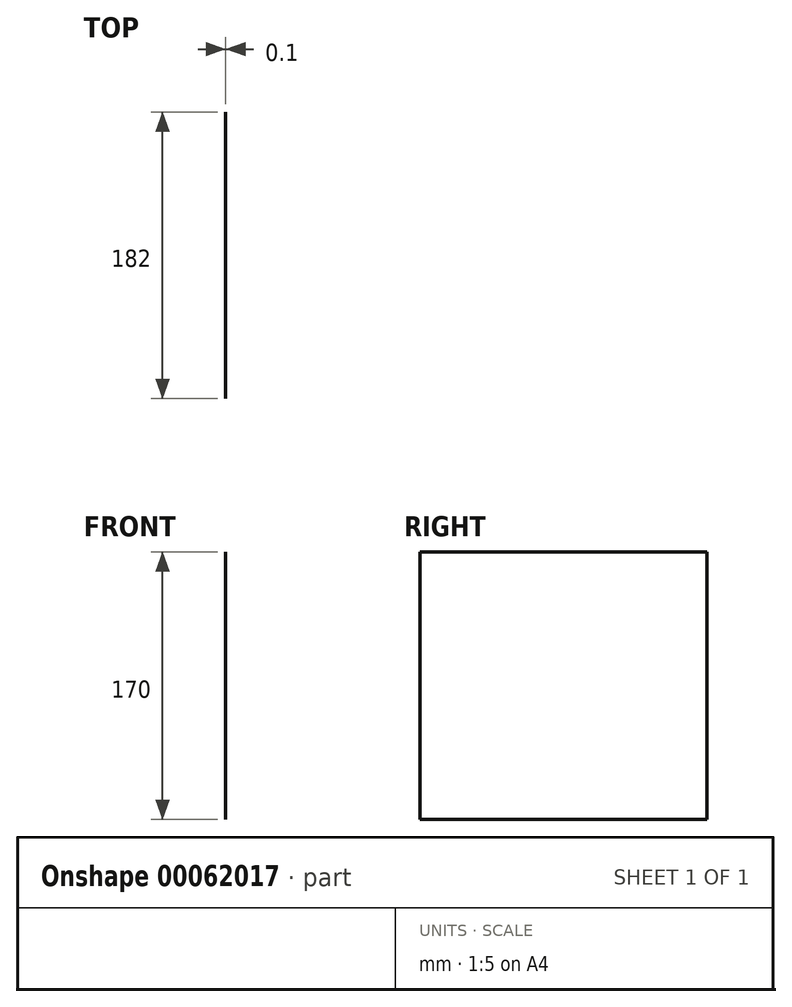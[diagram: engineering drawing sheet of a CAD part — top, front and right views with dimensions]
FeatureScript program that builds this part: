
annotation { "Feature Type Name" : "Feature", "Feature Type Description" : "" }
export const myFeature = defineFeature(function(context is Context, id is Id, definition is map)
    precondition{}
    {
        {
            var Q0;
            Q0=qCreatedBy(makeId("Front.planeOp"),FACE);
            var sketch = newSketch(context, id + "F0", { "sketchPlane" : qUnion([Q0])});
            skLineSegment(sketch, "E0", {"start": v(0, 72.34) * mm, "end": v(0, -97.66) * mm, "construction": true});
            skLineSegment(sketch, "E1.bottom", {"start": v(0, 72.34) * mm, "end": v(-0.1, 72.34) * mm});
            skLineSegment(sketch, "E1.top", {"start": v(0, -97.66) * mm, "end": v(-0.1, -97.66) * mm});
            skLineSegment(sketch, "E1.left", {"start": v(0, 72.34) * mm, "end": v(0, -97.66) * mm});
            skLineSegment(sketch, "E1.right", {"start": v(-0.1, 72.34) * mm, "end": v(-0.1, -97.66) * mm});
            skSolve(sketch);
        }
        {
            var Q0;
            Q0 = qSketchRegion(id + "F0", true);
            var Q1;
            Q1 = qConstructionFilter(qBodyType(qCreatedBy(id + "F0" ,EDGE), BodyType.WIRE), ConstructionObject.NO);
            extrude(context, id + "F1", {"entities" : qUnion([Q0]), "surfaceEntities" : qUnion([Q1]), "depth" : 57 * mm, "hasSecondDirection" : true, "secondDirectionOppositeDirection" : true, "secondDirectionDepth" : 125 * mm});
        }
    });
